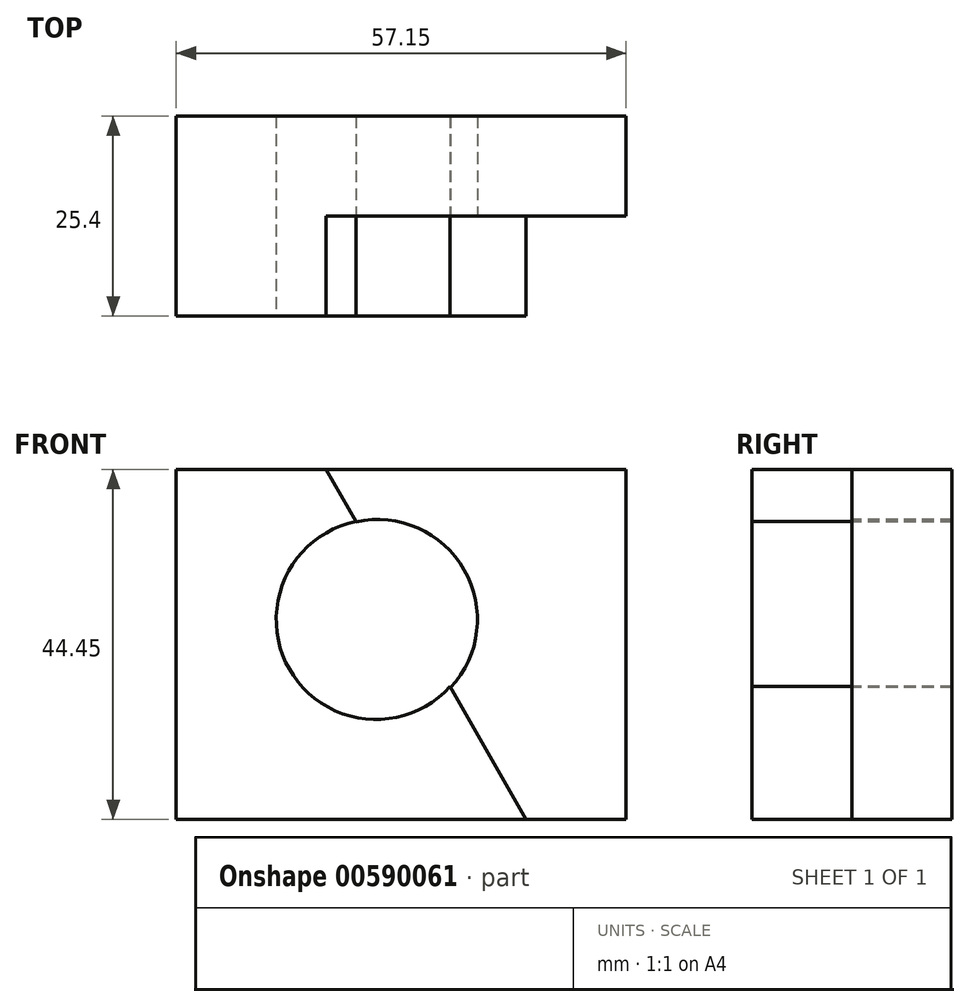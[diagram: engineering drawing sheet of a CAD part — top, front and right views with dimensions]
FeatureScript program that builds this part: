
annotation { "Feature Type Name" : "Feature", "Feature Type Description" : "" }
export const myFeature = defineFeature(function(context is Context, id is Id, definition is map)
    precondition{}
    {
        {
            var Q0;
            Q0=qCreatedBy(makeId("Front.planeOp"),FACE);
            var sketch = newSketch(context, id + "F0", { "sketchPlane" : qUnion([Q0])});
            skLineSegment(sketch, "E0.bottom", {"start": v(-60.37, 55.34) * mm, "end": v(-3.22, 55.34) * mm});
            skLineSegment(sketch, "E0.top", {"start": v(-60.37, 10.89) * mm, "end": v(-3.22, 10.89) * mm});
            skLineSegment(sketch, "E0.left", {"start": v(-60.37, 55.34) * mm, "end": v(-60.37, 10.89) * mm});
            skLineSegment(sketch, "E0.right", {"start": v(-3.22, 55.34) * mm, "end": v(-3.22, 10.89) * mm});
            skSolve(sketch);
        }
        {
            var Q0;
            Q0=makeQuery(id+"F0.imprint","IMPRINT",FACE,{"disambiguationData":[TD([[makeQuery(id+"F0.imprint","IMPRINT",EDGE,{"derivedFrom":sQuery(id+"F0.wireOp",EDGE,"E0.bottom")}),-1.0]])]});
            extrude(context, id + "F1", {"entities" : qUnion([Q0]), "depth" : 25.4 * mm, "offsetDistance" : 25.4 * mm});
        }
        {
            var Q0;
            Q0=makeQuery(id+"F1.opExtrude","CAP_FACE",FACE,{"disambiguationData":[OSD([sQuery(id+"F0.wireOp",EDGE,"E0.bottom"),sQuery(id+"F0.wireOp",EDGE,"E0.top"),sQuery(id+"F0.wireOp",EDGE,"E0.left"),sQuery(id+"F0.wireOp",EDGE,"E0.right")])],"isStart":false});
            var sketch = newSketch(context, id + "F2", { "sketchPlane" : qUnion([Q0])});
            skLineSegment(sketch, "E1", {"start": v(-41.32, 55.34) * mm, "end": v(-15.92, 10.89) * mm});
            skSolve(sketch);
        }
        {
            var Q0;
            {var subQ0=sQuery(id+"F2.wireOp",EDGE,"E1");Q0=makeQuery(id+"F2.imprint","IMPRINT",FACE,{"disambiguationData":[TD([[makeQuery(id+"F2.imprint","IMPRINT",EDGE,{"derivedFrom":subQ0}),1.0]])]});}
            extrude(context, id + "F3", {"entities" : qUnion([Q0]), "operationType" : NewBodyOperationType.REMOVE, "oppositeDirection" : true, "depth" : 12.7 * mm, "offsetDistance" : 25.4 * mm});
        }
        {
            var Q0;
            Q0=makeQuery(id+"F3.boolean.opBoolean","COPY",FACE,{"derivedFrom":makeQuery(id+"F3.opExtrude","CAP_FACE",FACE,{"disambiguationData":[OSD([sQuery(id+"F0.wireOp",EDGE,"E0.bottom"),sQuery(id+"F0.wireOp",EDGE,"E0.top"),sQuery(id+"F0.wireOp",EDGE,"E0.right"),sQuery(id+"F2.wireOp",EDGE,"E1")])],"isStart":false})});
            var sketch = newSketch(context, id + "F4", { "sketchPlane" : qUnion([Q0])});
            skCircle(sketch, "E2", {"center": v(-34.8, 36.29) * mm, "radius": 12.7 * mm});
            skSolve(sketch);
        }
        {
            var Q0;
            {var subQ0=sQuery(id+"F4.wireOp",EDGE,"E2");var subQ1=makeQuery(id+"F3.boolean.opBoolean","COPY",EDGE,{"derivedFrom":makeQuery(id+"F3.opExtrude","CAP_EDGE",EDGE,{"disambiguationData":[OSD([sQuery(id+"F2.wireOp",EDGE,"E1")])],"isStart":false})});var subQ2=makeQuery(id+"F4.imprint","INTERSECT",VERTEX,{"disambiguationData":[OD(0.0)],"derivedFrom":[subQ1,subQ0]});Q0=makeQuery(id+"F4.imprint","IMPRINT",FACE,{"disambiguationData":[TD([[makeQuery(id+"F4.imprint","IMPRINT",EDGE,{"disambiguationData":[TD([[subQ2,1.0]])],"derivedFrom":subQ0}),1.0]])]});}
            extrude(context, id + "F5", {"entities" : qUnion([Q0]), "operationType" : NewBodyOperationType.REMOVE, "oppositeDirection" : true, "depth" : 25.4 * mm, "offsetDistance" : 25.4 * mm});
        }
        {
            var Q0;
            Q0=makeQuery(id+"F1.opExtrude","CAP_FACE",FACE,{"disambiguationData":[OSD([sQuery(id+"F0.wireOp",EDGE,"E0.bottom"),sQuery(id+"F0.wireOp",EDGE,"E0.top"),sQuery(id+"F0.wireOp",EDGE,"E0.left"),sQuery(id+"F0.wireOp",EDGE,"E0.right")])],"isStart":false});
            var sketch = newSketch(context, id + "F6", { "sketchPlane" : qUnion([Q0])});
            skCircle(sketch, "E3", {"center": v(-34.97, 36.29) * mm, "radius": 12.7 * mm});
            skSolve(sketch);
        }
        {
            var Q0;
            {var subQ0=sQuery(id+"F6.wireOp",EDGE,"E3");var subQ1=makeQuery(id+"F3.boolean.opBoolean","COPY",EDGE,{"derivedFrom":makeQuery(id+"F3.opExtrude","CAP_EDGE",EDGE,{"disambiguationData":[OSD([sQuery(id+"F2.wireOp",EDGE,"E1")])],"isStart":true})});var subQ2=makeQuery(id+"F6.imprint","INTERSECT",VERTEX,{"disambiguationData":[OD(0.0)],"derivedFrom":[subQ1,subQ0]});Q0=makeQuery(id+"F6.imprint","IMPRINT",FACE,{"disambiguationData":[TD([[makeQuery(id+"F6.imprint","IMPRINT",EDGE,{"disambiguationData":[TD([[subQ2,-1.0]])],"derivedFrom":subQ0}),1.0]])]});}
            extrude(context, id + "F7", {"entities" : qUnion([Q0]), "operationType" : NewBodyOperationType.REMOVE, "oppositeDirection" : true, "depth" : 25.4 * mm, "offsetDistance" : 25.4 * mm});
        }
    });
